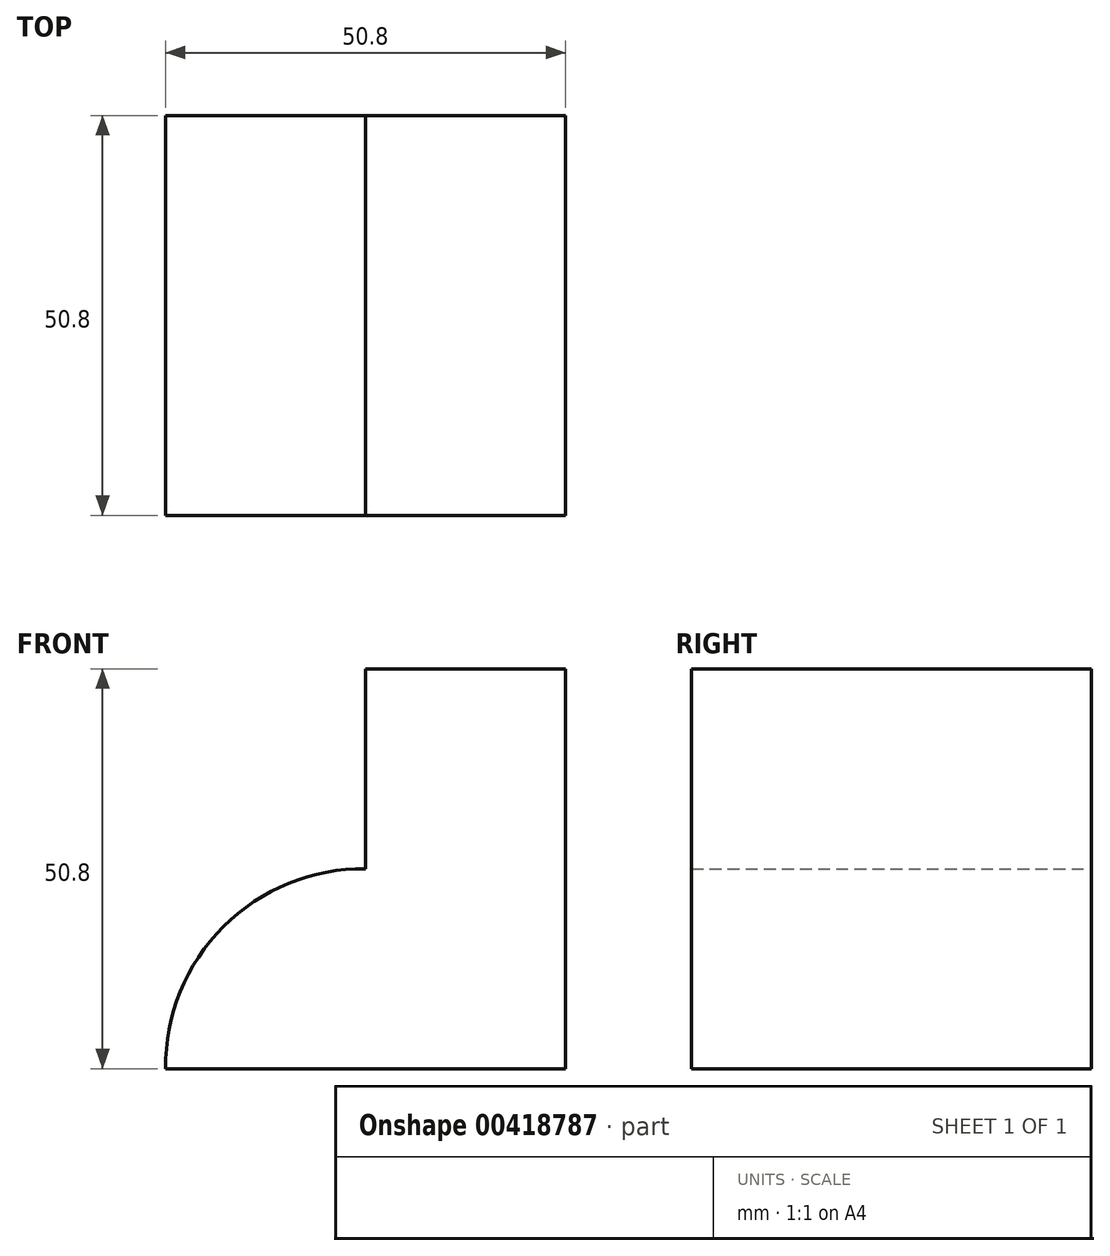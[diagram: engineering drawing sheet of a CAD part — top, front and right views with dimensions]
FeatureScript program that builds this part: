
annotation { "Feature Type Name" : "Feature", "Feature Type Description" : "" }
export const myFeature = defineFeature(function(context is Context, id is Id, definition is map)
    precondition{}
    {
        {
            var Q0;
            Q0=qCreatedBy(makeId("Front.planeOp"),FACE);
            var sketch = newSketch(context, id + "F0", { "sketchPlane" : qUnion([Q0])});
            skLineSegment(sketch, "E0", {"start": v(0, 0) * mm, "end": v(25.4, 0) * mm});
            skLineSegment(sketch, "E1", {"start": v(25.4, 0) * mm, "end": v(25.4, -50.8) * mm});
            skLineSegment(sketch, "E2", {"start": v(25.4, -50.8) * mm, "end": v(-25.4, -50.8) * mm});
            skLineSegment(sketch, "E3", {"start": v(0, 0) * mm, "end": v(0, -25.4) * mm});
            skArc(sketch, "E4", {"start": v(0, -25.4) * mm, "mid": v(-18.05, -32.75) * mm, "end": v(-25.4, -50.8) * mm});
            skSolve(sketch);
        }
        {
            var Q0;
            Q0=makeQuery(id+"F0.imprint","IMPRINT",FACE,{"disambiguationData":[TD([[makeQuery(id+"F0.imprint","IMPRINT",EDGE,{"derivedFrom":sQuery(id+"F0.wireOp",EDGE,"E0")}),-1.0]])]});
            extrude(context, id + "F1", {"entities" : qUnion([Q0]), "depth" : 50.8 * mm});
        }
    });
